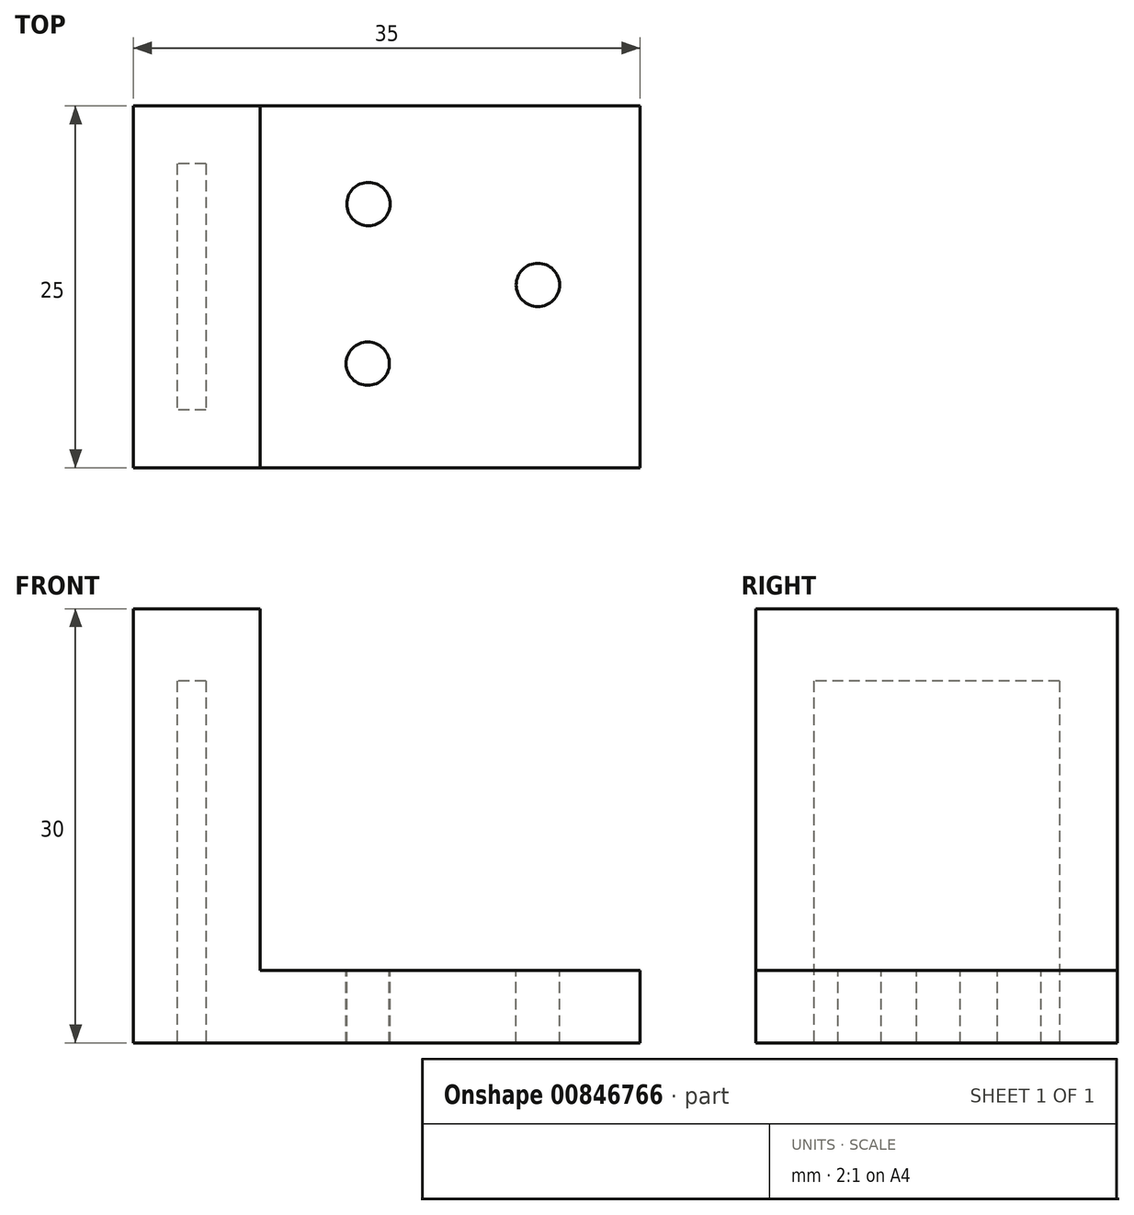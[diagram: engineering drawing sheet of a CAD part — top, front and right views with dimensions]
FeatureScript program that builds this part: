
annotation { "Feature Type Name" : "Feature", "Feature Type Description" : "" }
export const myFeature = defineFeature(function(context is Context, id is Id, definition is map)
    precondition{}
    {
        {
            var Q0;
            Q0=qCreatedBy(makeId("Front.planeOp"),FACE);
            var sketch = newSketch(context, id + "F0", { "sketchPlane" : qUnion([Q0])});
            skLineSegment(sketch, "E0", {"start": v(-40.34, -1.85) * mm, "end": v(-40.34, 28.15) * mm});
            skLineSegment(sketch, "E1", {"start": v(-40.34, 28.15) * mm, "end": v(-31.59, 28.15) * mm});
            skLineSegment(sketch, "E2", {"start": v(-31.59, 28.15) * mm, "end": v(-31.59, 3.15) * mm});
            skLineSegment(sketch, "E3", {"start": v(-31.59, 3.15) * mm, "end": v(-5.34, 3.15) * mm});
            skLineSegment(sketch, "E4", {"start": v(-5.34, 3.15) * mm, "end": v(-5.34, -1.85) * mm});
            skLineSegment(sketch, "E5", {"start": v(-5.34, -1.85) * mm, "end": v(-40.34, -1.85) * mm});
            skSolve(sketch);
        }
        {
            var Q0;
            Q0=makeQuery(id+"F0.imprint","IMPRINT",FACE,{"disambiguationData":[TD([[makeQuery(id+"F0.imprint","IMPRINT",EDGE,{"derivedFrom":sQuery(id+"F0.wireOp",EDGE,"E0")}),-1.0]])]});
            extrude(context, id + "F1", {"entities" : qUnion([Q0]), "depth" : 25 * mm, "offsetDistance" : 25 * mm});
        }
        {
            var Q0;
            Q0=makeQuery(id+"F1.opExtrude","SWEPT_FACE",FACE,{"disambiguationData":[OSD([sQuery(id+"F0.wireOp",EDGE,"E5")])]});
            var sketch = newSketch(context, id + "F2", { "sketchPlane" : qUnion([Q0])});
            skLineSegment(sketch, "E6.bottom", {"start": v(-35.34, 4) * mm, "end": v(-37.34, 4) * mm});
            skLineSegment(sketch, "E6.top", {"start": v(-35.34, 21) * mm, "end": v(-37.34, 21) * mm});
            skLineSegment(sketch, "E6.left", {"start": v(-35.34, 4) * mm, "end": v(-35.34, 21) * mm});
            skLineSegment(sketch, "E6.right", {"start": v(-37.34, 4) * mm, "end": v(-37.34, 21) * mm});
            skSolve(sketch);
        }
        {
            var Q0;
            Q0=makeQuery(id+"F2.imprint","IMPRINT",FACE,{"disambiguationData":[TD([[makeQuery(id+"F2.imprint","IMPRINT",EDGE,{"derivedFrom":sQuery(id+"F2.wireOp",EDGE,"E6.bottom")}),-1.0]])]});
            var Q1;
            Q1=makeQuery(id+"F1.opExtrude","SWEPT_FACE",FACE,{"disambiguationData":[OSD([sQuery(id+"F0.wireOp",EDGE,"E1")])]});
            extrude(context, id + "F3", {"entities" : qUnion([Q0, Q1]), "operationType" : NewBodyOperationType.REMOVE, "oppositeDirection" : true, "depth" : 25 * mm, "offsetDistance" : 25 * mm});
        }
        {
            var Q0;
            Q0=makeQuery(id+"F1.opExtrude","SWEPT_FACE",FACE,{"disambiguationData":[OSD([sQuery(id+"F0.wireOp",EDGE,"E3")])]});
            var sketch = newSketch(context, id + "F4", { "sketchPlane" : qUnion([Q0])});
            skCircle(sketch, "E7", {"center": v(-24.15, -17.8) * mm, "radius": 1.5 * mm});
            skCircle(sketch, "E8", {"center": v(-24.1, -6.78) * mm, "radius": 1.5 * mm});
            skCircle(sketch, "E9", {"center": v(-12.39, -12.37) * mm, "radius": 1.5 * mm});
            skSolve(sketch);
        }
        {
            var Q0;
            Q0=makeQuery(id+"F4.imprint","IMPRINT",FACE,{"disambiguationData":[TD([[makeQuery(id+"F4.imprint","IMPRINT",EDGE,{"derivedFrom":sQuery(id+"F4.wireOp",EDGE,"E9")}),1.0]])]});
            var Q1;
            Q1=makeQuery(id+"F4.imprint","IMPRINT",FACE,{"disambiguationData":[TD([[makeQuery(id+"F4.imprint","IMPRINT",EDGE,{"derivedFrom":sQuery(id+"F4.wireOp",EDGE,"E7")}),1.0]])]});
            var Q2;
            Q2=makeQuery(id+"F4.imprint","IMPRINT",FACE,{"disambiguationData":[TD([[makeQuery(id+"F4.imprint","IMPRINT",EDGE,{"derivedFrom":sQuery(id+"F4.wireOp",EDGE,"E8")}),1.0]])]});
            extrude(context, id + "F5", {"entities" : qUnion([Q0, Q1, Q2]), "operationType" : NewBodyOperationType.REMOVE, "oppositeDirection" : true, "depth" : 25 * mm, "offsetDistance" : 25 * mm});
        }
    });
